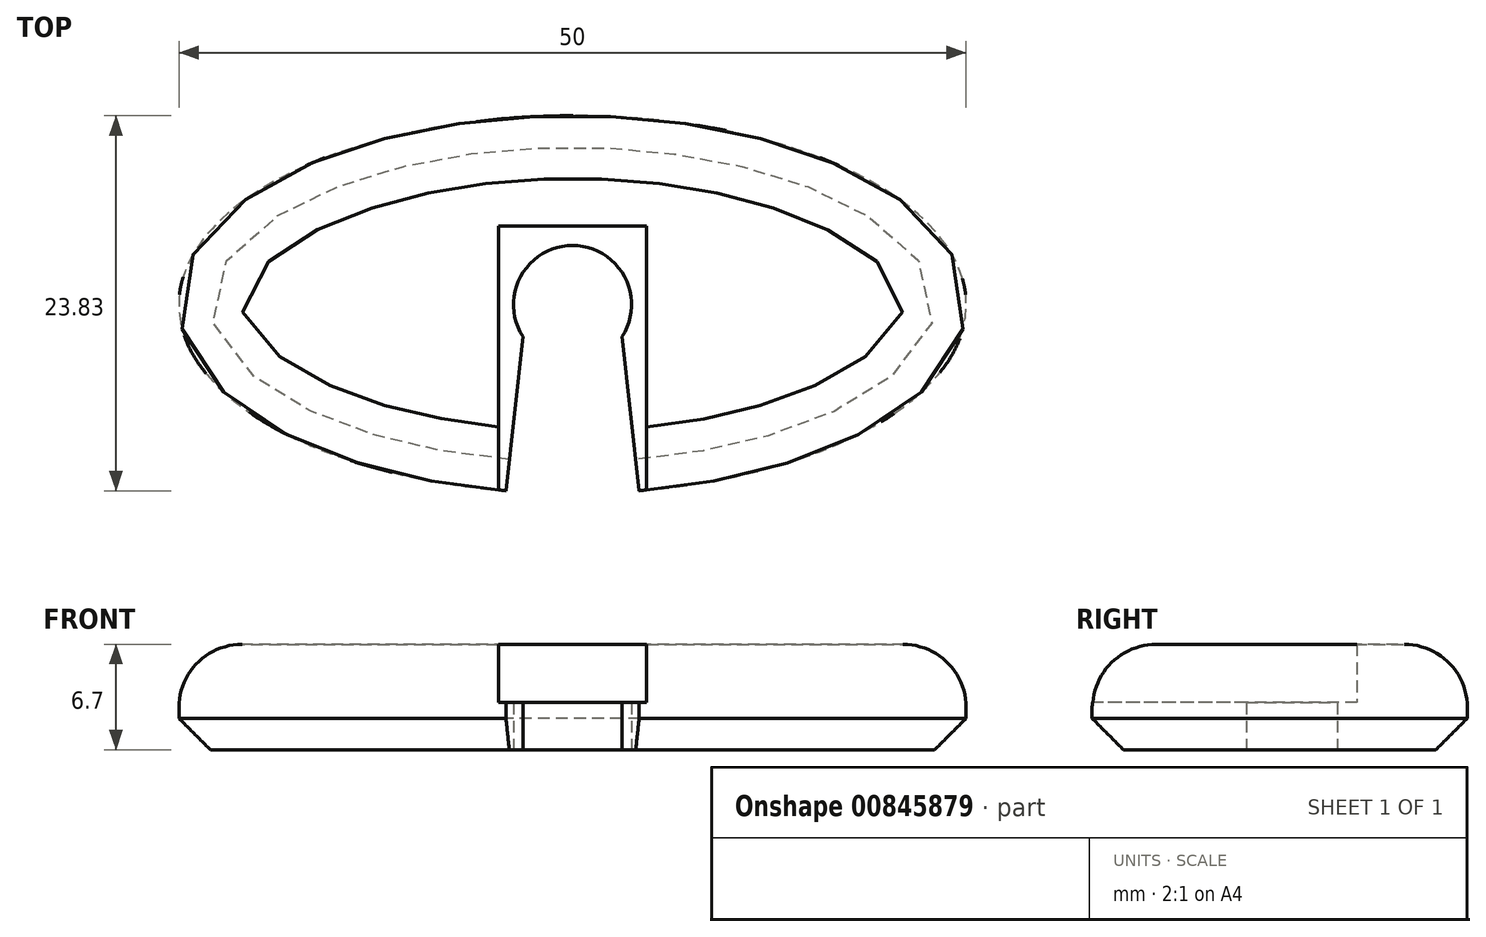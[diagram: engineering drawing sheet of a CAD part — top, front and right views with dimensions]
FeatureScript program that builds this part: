
annotation { "Feature Type Name" : "Feature", "Feature Type Description" : "" }
export const myFeature = defineFeature(function(context is Context, id is Id, definition is map)
    precondition{}
    {
        {
            var Q0;
            Q0=qCreatedBy(makeId("Top.planeOp"),FACE);
            var sketch = newSketch(context, id + "F0", { "sketchPlane" : qUnion([Q0])});
            skCircle(sketch, "E0", {"center": v(0, 0) * mm, "radius": 3.75 * mm});
            skLineSegment(sketch, "E1.bottom", {"start": v(-25, 12) * mm, "end": v(25, 12) * mm});
            skLineSegment(sketch, "E1.top", {"start": v(-25, -12) * mm, "end": v(25, -12) * mm});
            skLineSegment(sketch, "E1.left", {"start": v(-25, 12) * mm, "end": v(-25, -12) * mm});
            skLineSegment(sketch, "E1.right", {"start": v(25, 12) * mm, "end": v(25, -12) * mm});
            skLineSegment(sketch, "E2", {"start": v(-3.15, -2.03) * mm, "end": v(-4.25, -12) * mm});
            skLineSegment(sketch, "E3", {"start": v(3.15, -2.03) * mm, "end": v(4.25, -12) * mm});
            skLineSegment(sketch, "E4.bottom", {"start": v(-4.7, 5) * mm, "end": v(4.7, 5) * mm});
            skLineSegment(sketch, "E4.top", {"start": v(-4.7, -12) * mm, "end": v(4.7, -12) * mm});
            skLineSegment(sketch, "E4.left", {"start": v(-4.7, 5) * mm, "end": v(-4.7, -12) * mm});
            skLineSegment(sketch, "E4.right", {"start": v(4.7, 5) * mm, "end": v(4.7, -12) * mm});
            skPoint(sketch, "E4.middle", {"position": v(0, -3.5) * mm});
            skEllipse(sketch, "E5", {"center": v(0, 0) * mm, "majorRadius": 25 * mm, "minorRadius": 12 * mm, "majorAxis": v(-1, 0)});
            skSolve(sketch);
        }
        {
            var Q0;
            {var subQ5=sQuery(id+"F0.wireOp",EDGE,"E4.bottom");Q0=makeQuery(id+"F0.imprint","IMPRINT",FACE,{"disambiguationData":[TD([[makeQuery(id+"F0.imprint","IMPRINT",EDGE,{"derivedFrom":subQ5}),1.0]])]});}
            var Q1;
            {var subQ0=sQuery(id+"F0.wireOp",EDGE,"E4.bottom");Q1=makeQuery(id+"F0.imprint","IMPRINT",FACE,{"disambiguationData":[TD([[makeQuery(id+"F0.imprint","IMPRINT",EDGE,{"derivedFrom":subQ0}),-1.0]])]});}
            var Q2;
            {var subQ1=sQuery(id+"F0.wireOp",EDGE,"E0");var subQ6=sQuery(id+"F0.wireOp",EDGE,"E2");var subQ8=makeQuery(id+"F0.imprint","INTERSECT",VERTEX,{"derivedFrom":[subQ1,subQ6]});Q2=makeQuery(id+"F0.imprint","IMPRINT",FACE,{"disambiguationData":[TD([[makeQuery(id+"F0.imprint","IMPRINT",EDGE,{"disambiguationData":[TD([[subQ8,-1.0]])],"derivedFrom":subQ1}),-1.0]])]});}
            var Q3;
            {var subQ0=sQuery(id+"F0.wireOp",EDGE,"E0");var subQ1=makeQuery(id+"F0.imprint","INTERSECT",VERTEX,{"derivedFrom":[subQ0,sQuery(id+"F0.wireOp",EDGE,"E2")]});Q3=makeQuery(id+"F0.imprint","IMPRINT",FACE,{"disambiguationData":[TD([[makeQuery(id+"F0.imprint","IMPRINT",EDGE,{"disambiguationData":[TD([[subQ1,-1.0]])],"derivedFrom":subQ0}),1.0]])]});}
            extrude(context, id + "F1", {"entities" : qUnion([Q0, Q1, Q2, Q3]), "depth" : 6.7 * mm, "offsetDistance" : 25 * mm});
        }
        {
            var Q0;
            Q0=makeQuery(id+"F1.opExtrude","CAP_FACE",FACE,{"disambiguationData":[OSD([sQuery(id+"F0.wireOp",EDGE,"E5")])],"isStart":false});
            fillet(context, id + "F2", {"entities" : qUnion([Q0]), "radius" : 4 * mm, "tangentPropagation" : true, "allowEdgeOverflow" : false});
        }
        {
            var Q0;
            Q0=makeQuery(id+"F1.opExtrude","CAP_EDGE",EDGE,{"disambiguationData":[OSD([sQuery(id+"F0.wireOp",EDGE,"E5")])],"isStart":true});
            chamfer(context, id + "F3", {"entities" : qUnion([Q0]), "width" : 2 * mm, "tangentPropagation" : true});
        }
        {
            var Q0;
            {var subQ0=sQuery(id+"F0.wireOp",EDGE,"E0");var subQ1=makeQuery(id+"F0.imprint","INTERSECT",VERTEX,{"derivedFrom":[subQ0,sQuery(id+"F0.wireOp",EDGE,"E2")]});Q0=makeQuery(id+"F0.imprint","IMPRINT",FACE,{"disambiguationData":[TD([[makeQuery(id+"F0.imprint","IMPRINT",EDGE,{"disambiguationData":[TD([[subQ1,-1.0]])],"derivedFrom":subQ0}),1.0]])]});}
            var Q1;
            {var subQ1=sQuery(id+"F0.wireOp",EDGE,"E0");var subQ6=sQuery(id+"F0.wireOp",EDGE,"E2");var subQ8=makeQuery(id+"F0.imprint","INTERSECT",VERTEX,{"derivedFrom":[subQ1,subQ6]});Q1=makeQuery(id+"F0.imprint","IMPRINT",FACE,{"disambiguationData":[TD([[makeQuery(id+"F0.imprint","IMPRINT",EDGE,{"disambiguationData":[TD([[subQ8,-1.0]])],"derivedFrom":subQ1}),-1.0]])]});}
            extrude(context, id + "F4", {"entities" : qUnion([Q0, Q1]), "operationType" : NewBodyOperationType.REMOVE, "depth" : 25 * mm, "offsetDistance" : 25 * mm});
        }
        {
            var Q0;
            {var subQ0=sQuery(id+"F0.wireOp",EDGE,"E4.bottom");Q0=makeQuery(id+"F0.imprint","IMPRINT",FACE,{"disambiguationData":[TD([[makeQuery(id+"F0.imprint","IMPRINT",EDGE,{"derivedFrom":subQ0}),-1.0]])]});}
            extrude(context, id + "F5", {"entities" : qUnion([Q0]), "operationType" : NewBodyOperationType.REMOVE, "depth" : 10 * mm, "offsetDistance" : 25 * mm, "hasSecondDirection" : true, "secondDirectionOppositeDirection" : false, "secondDirectionDepth" : 3 * mm});
        }
    });
